# Revit family: 6098_Kunststoffrohranschlüsse G 3_4 für PE-X & PB-Kunststoffrohre
name_source: partatom
category: Rohrformteile
units: mm (PartAtom-declared; Revit-internal decimal feet)

## family parameters
Arbeitsebenenbasiert = Nein
Beim Laden mit Abzugskörper schneiden = Nein
Bemaßung runder Anschluss = Durchmesser verwenden
Gemeinsam genutzt = Nein
Immer vertikal = Ja
OmniClass-Nummer = 23.65.55.14
OmniClass-Titel = Valves for Liquid Services
Teiletyp = Verbindung

## types (1)
- 20x3.4
    20x3.4 = Ja
    Anwendungsgebiet = Die Kunststoffrohranschlüsse sind geeignet für Heizungsinstallationen der Anwendungsklassen 1,2, 4 und 5, gemäß ISO 10508, für Rohre aus PE-X (EN ISO 15875) und PE-RT (EN ISO 22391).
Die Vorgaben der Rohrhersteller bezüglich Druck und Temperatur sind zu beachten.
Der Kunststoffrohranschluss stellt eine absolut sichere Verbindung zwischen Rohr und Ventilgehäuse dar.
Diese Verbindung kann bei Bedarf jederzeit gelöst werden.
Eine einwandfreie Dichtheit ist auf Dauer nur dann gegeben, wenn die Montage ordnungsgemäß nach HERZ-Montageanleitung durchgeführt wurde.
    Ausführung = 6098 G 3/4 - 20mm:
Kunststoffrohranschluss mit Doppel-O-Ring, bestehend aus Schlauchtülle mit Konus, Schlauchklemmring und Überwurfmutter G 3/4 mit Konus.
    Bestellnummer = 1609819
    Hersteller = HERZ Armaturen Ges.m.b.H.
    Hinweiß zum Werkstoff = Gemäß Art 33 der REACH-Verordnung (EG Nr. 1907/2006) sind wir verpflichtet, darauf hinzuweisen, dass der Stoff Blei auf der SVHC-Liste geführt wird und dass alle aus Messing bestehenden Bauteile, die in unseren Erzeugnissen verarbeitet sind, mehr als 0,1 % (w/w) Blei (CAS: 7439-92-1 / EINECS: 231-100-4) enthalten.
Da Blei als Legierungsbestandteil fest gebunden ist, sind keine Expositionen zu erwarten und daher sind keine zusätzlichen Angaben zur sicheren Verwendung notwendig.
    KL00 = 8 mm  [stored 0.0262467 ft]
    Klemmring = CW617N
    MD01 = 12 mm  [stored 0.0393701 ft]
    Max. Betriebsdruck = 1000000.0 Pa
    Max. Betriebstemperatur = 95 °C
    Medium = Heizungswasser nach ÖNORM H5195 oder VDI- Richtlinie 2035.
Die Verwendung von Ethylen- oder Propyleneglykol in einem Mischungsverhältnis 25-50% ist zulässig.
    Mutter = CW617N, G 3/4
    Nennweite = 20 mm  [stored 0.0656168 ft]
    O-Ring = EPDM
    S01 = 5 mm  [stored 0.0164042 ft]
    S02 = 5 mm  [stored 0.0164042 ft]
    SCRNCODE = 07;01;02
    SCRNSEQ = AWI;AWI_TYP="1001";2
    TD00 = 9 mm  [stored 0.0295276 ft]
    Tülle = CW617N
    URL = www.herz-armaturen.at
    Vorgabe-Ansicht = 0 mm  [stored 0 ft]

note: [stored X ft] marks values corroborated as IEEE doubles in the binary element streams (Revit-internal decimal feet)
